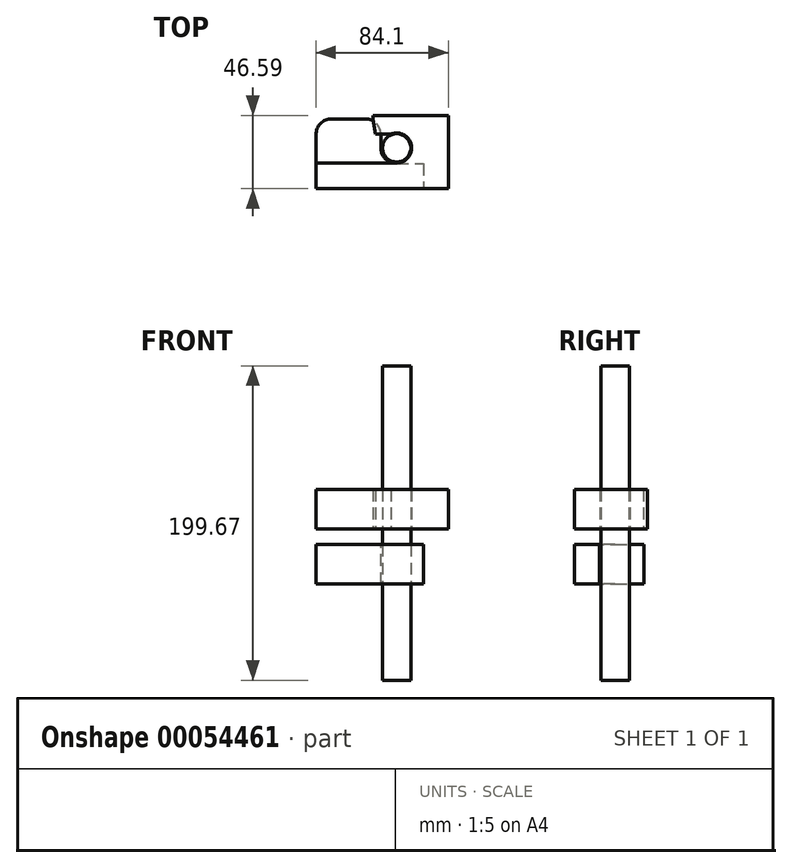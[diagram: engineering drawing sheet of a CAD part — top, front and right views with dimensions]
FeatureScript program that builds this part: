
annotation { "Feature Type Name" : "Feature", "Feature Type Description" : "" }
export const myFeature = defineFeature(function(context is Context, id is Id, definition is map)
    precondition{}
    {
        {
            var Q0;
            Q0=qCreatedBy(makeId("Top.planeOp"),FACE);
            var sketch = newSketch(context, id + "F0", { "sketchPlane" : qUnion([Q0])});
            skLineSegment(sketch, "E0.top", {"start": v(-6.56, 44.38) * mm, "end": v(-27.8, 44.38) * mm});
            skLineSegment(sketch, "E0.left", {"start": v(3.44, 25.92) * mm, "end": v(3.44, 34.38) * mm});
            skLineSegment(sketch, "E0.right", {"start": v(-37.8, 0) * mm, "end": v(-37.8, 34.38) * mm});
            skLineSegment(sketch, "E1.bottom", {"start": v(13.44, 15.92) * mm, "end": v(30.54, 15.92) * mm});
            skLineSegment(sketch, "E1.right", {"start": v(30.54, 15.92) * mm, "end": v(30.54, 0) * mm});
            skLineSegment(sketch, "E2", {"start": v(-37.8, 0) * mm, "end": v(30.54, 0) * mm});
            skPoint(sketch, "E3.visualSharp", {"position": v(3.44, 15.92) * mm});
            skArc(sketch, "E3.filletArc", {"start": v(3.44, 25.92) * mm, "mid": v(6.37, 18.85) * mm, "end": v(13.44, 15.92) * mm});
            skPoint(sketch, "E4.visualSharp", {"position": v(3.44, 44.38) * mm});
            skArc(sketch, "E4.filletArc", {"start": v(3.44, 34.38) * mm, "mid": v(0.51, 41.45) * mm, "end": v(-6.56, 44.38) * mm});
            skPoint(sketch, "E5.visualSharp", {"position": v(-37.8, 44.38) * mm});
            skArc(sketch, "E5.filletArc", {"start": v(-27.8, 44.38) * mm, "mid": v(-34.86, 41.45) * mm, "end": v(-37.8, 34.38) * mm});
            skCircle(sketch, "E6", {"center": v(13.44, 25.92) * mm, "radius": 9 * mm});
            skSolve(sketch);
        }
        {
            var Q0;
            Q0=qCreatedBy(makeId("Top.planeOp"),FACE);
            cPlane(context, id + "F1", {"entities" : qUnion([Q0]), "cplaneType" : CPlaneType.OFFSET, "offset" : 10 * mm, "width" : 150 * mm, "height" : 150 * mm});
        }
        {
            var Q0;
            Q0=qCreatedBy(id+"F1.planeOp",FACE);
            var sketch = newSketch(context, id + "F2", { "sketchPlane" : qUnion([Q0])});
            skLineSegment(sketch, "E7", {"start": v(-37.88, 0) * mm, "end": v(-37.88, 16.42) * mm});
            skLineSegment(sketch, "E8", {"start": v(-37.88, 16.42) * mm, "end": v(13.44, 16.42) * mm});
            skLineSegment(sketch, "E9", {"start": v(-37.88, 0) * mm, "end": v(46.22, 0) * mm});
            skLineSegment(sketch, "E10", {"start": v(46.22, 0) * mm, "end": v(46.22, 46.6) * mm});
            skLineSegment(sketch, "E11", {"start": v(46.22, 46.6) * mm, "end": v(-1.6, 46.6) * mm});
            skLineSegment(sketch, "E12", {"start": v(-1.6, 46.6) * mm, "end": v(-1.6, 43.95) * mm});
            skLineSegment(sketch, "E13", {"start": v(-1.6, 43.95) * mm, "end": v(0, 34.73) * mm});
            skLineSegment(sketch, "E14", {"start": v(0, 34.73) * mm, "end": v(9.88, 34.73) * mm});
            skArc(sketch, "E15", {"start": v(13.44, 16.42) * mm, "mid": v(22.77, 27.73) * mm, "end": v(9.88, 34.73) * mm});
            skSolve(sketch);
        }
        {
            var Q0;
            Q0=makeQuery(id+"F0.imprint","IMPRINT",FACE,{"disambiguationData":[TD([[makeQuery(id+"F0.imprint","IMPRINT",EDGE,{"derivedFrom":sQuery(id+"F0.wireOp",EDGE,"E0.top")}),1.0]])]});
            extrude(context, id + "F3", {"entities" : qUnion([Q0]), "oppositeDirection" : true, "depth" : 25 * mm});
        }
        {
            var Q0;
            Q0=makeQuery(id+"F2.imprint","IMPRINT",FACE,{"disambiguationData":[TD([[makeQuery(id+"F2.imprint","IMPRINT",EDGE,{"derivedFrom":sQuery(id+"F2.wireOp",EDGE,"E7")}),-1.0]])]});
            extrude(context, id + "F4", {"entities" : qUnion([Q0]), "depth" : 25 * mm});
        }
        {
            var Q0;
            Q0=makeQuery(id+"F0.imprint","IMPRINT",FACE,{"disambiguationData":[TD([[makeQuery(id+"F0.imprint","IMPRINT",EDGE,{"derivedFrom":sQuery(id+"F0.wireOp",EDGE,"E6")}),1.0]])]});
            extrude(context, id + "F5", {"entities" : qUnion([Q0]), "depth" : 113.6 * mm, "hasSecondDirection" : true, "secondDirectionOppositeDirection" : true, "secondDirectionDepth" : 86.07 * mm});
        }
    });
